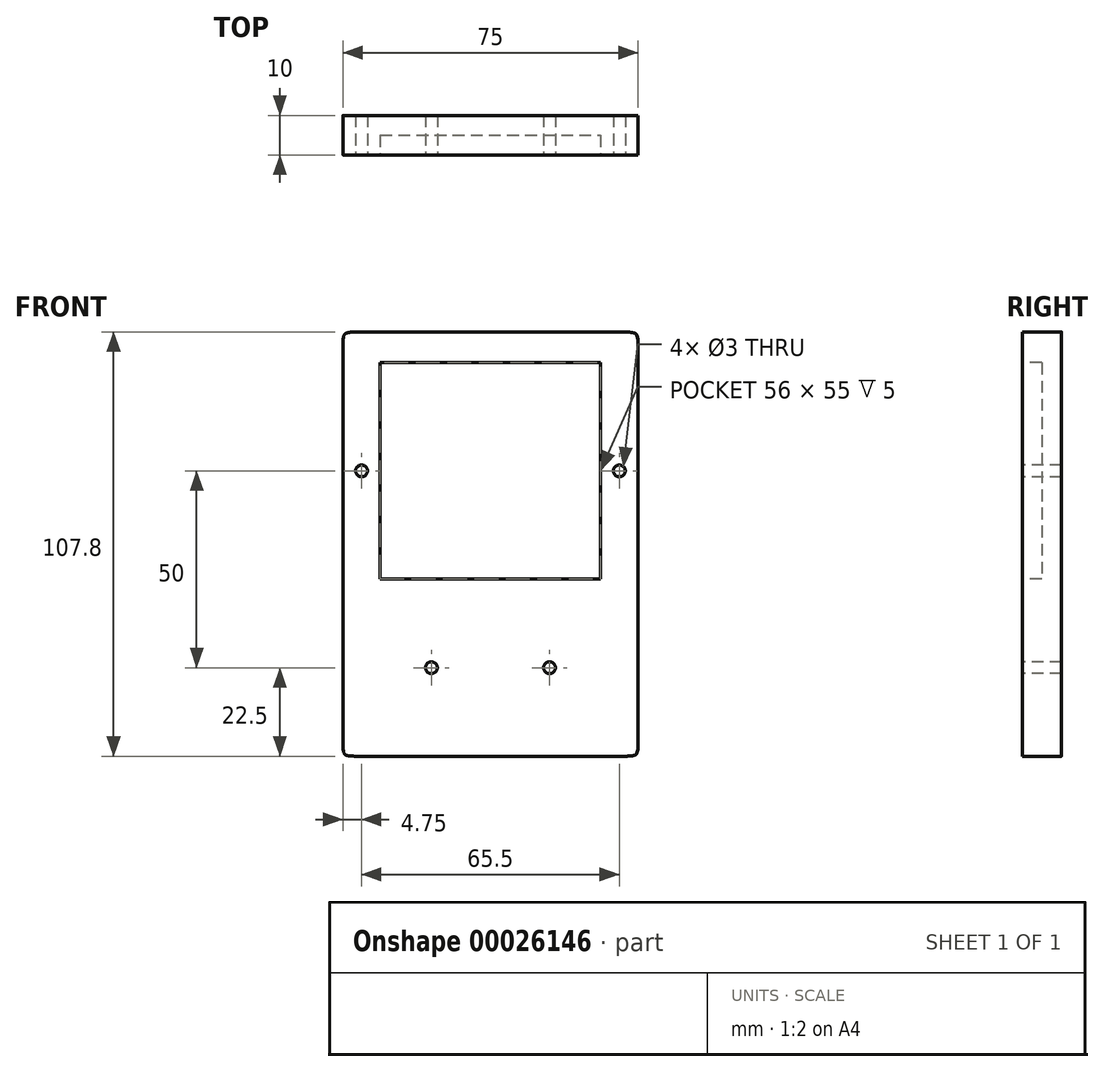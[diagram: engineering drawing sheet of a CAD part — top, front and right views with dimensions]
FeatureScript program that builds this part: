
annotation { "Feature Type Name" : "Feature", "Feature Type Description" : "" }
export const myFeature = defineFeature(function(context is Context, id is Id, definition is map)
    precondition{}
    {
        {
            var Q0;
            Q0=qCreatedBy(makeId("Front.planeOp"),FACE);
            var sketch = newSketch(context, id + "F0", { "sketchPlane" : qUnion([Q0])});
            skLineSegment(sketch, "E0.rect.top", {"start": v(37.5, 53.9) * mm, "end": v(-37.5, 53.9) * mm});
            skLineSegment(sketch, "E0.rect.left", {"start": v(37.5, -53.9) * mm, "end": v(37.5, 53.9) * mm});
            skLineSegment(sketch, "E0.rect.right", {"start": v(-37.5, -53.9) * mm, "end": v(-37.5, 53.9) * mm});
            skPoint(sketch, "E0.rect.middle", {"position": v(0, 0) * mm});
            skLineSegment(sketch, "E1", {"start": v(-37.5, 44.37) * mm, "end": v(37.5, 44.37) * mm, "construction": true});
            skLineSegment(sketch, "E2", {"start": v(37.5, 44.37) * mm, "end": v(-37.5, -44.37) * mm, "construction": true});
            skLineSegment(sketch, "E3", {"start": v(-37.5, -44.37) * mm, "end": v(37.5, -44.37) * mm, "construction": true});
            skPoint(sketch, "E4.rect.middle", {"position": v(-19.5, 44.37) * mm});
            skPoint(sketch, "E5.rect.middle", {"position": v(19.5, 44.37) * mm});
            skPoint(sketch, "E6.rect.middle", {"position": v(-19.5, -44.37) * mm});
            skPoint(sketch, "E7.rect.middle", {"position": v(19.5, -44.37) * mm});
            skLineSegment(sketch, "E8", {"start": v(0, -25) * mm, "end": v(0, 25) * mm, "construction": true});
            skLineSegment(sketch, "E9", {"start": v(-15, 0) * mm, "end": v(15, 0) * mm, "construction": true});
            skPoint(sketch, "E10.rect.middle", {"position": v(25.15, 0) * mm});
            skPoint(sketch, "E11.orphan", {"position": v(20.1, 30.91) * mm});
            skPoint(sketch, "E10.rect.right.end.orphan", {"position": v(30.2, 30.91) * mm});
            skPoint(sketch, "E10.rect.bottom.end.orphan", {"position": v(30.2, -30.91) * mm});
            skPoint(sketch, "E10.rect.bottom.start.orphan", {"position": v(20.1, -30.91) * mm});
            skPoint(sketch, "E12.rect.middle", {"position": v(25.15, -0.46) * mm});
            skPoint(sketch, "E13.center.orphan", {"position": v(20.1, -31.37) * mm});
            skPoint(sketch, "E14.center.orphan", {"position": v(30.2, -31.37) * mm});
            skPoint(sketch, "E15.orphan", {"position": v(-4.5, 40.24) * mm});
            skPoint(sketch, "E4.rect.top.start.orphan", {"position": v(-4.5, 48.5) * mm});
            skPoint(sketch, "E16.orphan", {"position": v(-34.5, 48.5) * mm});
            skPoint(sketch, "E4.rect.right.start.orphan", {"position": v(-34.5, 40.25) * mm});
            skPoint(sketch, "E5.rect.top.start.orphan", {"position": v(4.5, 48.5) * mm});
            skPoint(sketch, "E17.orphan", {"position": v(4.5, 40.24) * mm});
            skPoint(sketch, "E18.orphan", {"position": v(34.5, 48.5) * mm});
            skPoint(sketch, "E5.rect.bottom.end.orphan", {"position": v(34.5, 40.24) * mm});
            skPoint(sketch, "E19.orphan", {"position": v(-4.5, -48.5) * mm});
            skPoint(sketch, "E6.rect.left.end.orphan", {"position": v(-4.5, -40.25) * mm});
            skPoint(sketch, "E20.orphan", {"position": v(-34.5, -40.25) * mm});
            skPoint(sketch, "E6.rect.right.start.orphan", {"position": v(-34.5, -48.5) * mm});
            skPoint(sketch, "E7.rect.right.end.orphan", {"position": v(4.5, -40.24) * mm});
            skPoint(sketch, "E21.trimOffspring.end.orphan", {"position": v(4.5, -48.5) * mm});
            skPoint(sketch, "E22.orphan", {"position": v(34.5, -48.5) * mm});
            skPoint(sketch, "E7.rect.top.start.orphan", {"position": v(34.5, -40.24) * mm});
            skLineSegment(sketch, "E23.rect.bottom", {"start": v(-28, 46.1) * mm, "end": v(28, 46.1) * mm});
            skLineSegment(sketch, "E23.rect.left", {"start": v(-28, 46.1) * mm, "end": v(-28, -8.9) * mm});
            skPoint(sketch, "E23.rect.middle", {"position": v(0, 18.6) * mm});
            skPoint(sketch, "E24.center.orphan", {"position": v(20.1, 30.45) * mm});
            skPoint(sketch, "E25.center.orphan", {"position": v(30.2, 30.45) * mm});
            skLineSegment(sketch, "E26", {"start": v(37.5, 18.6) * mm, "end": v(-37.5, 18.6) * mm, "construction": true});
            skLineSegment(sketch, "E27", {"start": v(-37.5, 18.6) * mm, "end": v(-28, 18.6) * mm, "construction": true});
            skCircle(sketch, "E28", {"center": v(-32.75, 18.6) * mm, "radius": 1.5 * mm});
            skCircle(sketch, "E29.MirrorC", {"center": v(32.75, 18.6) * mm, "radius": 1.5 * mm});
            skLineSegment(sketch, "E30", {"start": v(-28, -8.9) * mm, "end": v(28, -53.9) * mm, "construction": true});
            skPoint(sketch, "E31.start.orphan", {"position": v(28, -8.9) * mm});
            skPoint(sketch, "E0.rect.bottom.end.orphan", {"position": v(30.2, -53.9) * mm});
            skLineSegment(sketch, "E32", {"start": v(28, 46.1) * mm, "end": v(28, -8.9) * mm});
            skLineSegment(sketch, "E33", {"start": v(28, -8.9) * mm, "end": v(-28, -8.9) * mm});
            skLineSegment(sketch, "E34", {"start": v(-37.5, -53.9) * mm, "end": v(37.5, -53.9) * mm});
            skLineSegment(sketch, "E35", {"start": v(-28, 46.1) * mm, "end": v(-37.5, 53.9) * mm, "construction": true});
            skLineSegment(sketch, "E36", {"start": v(28, 46.1) * mm, "end": v(37.5, 53.9) * mm, "construction": true});
            skLineSegment(sketch, "E37", {"start": v(0, -8.9) * mm, "end": v(0, -53.9) * mm, "construction": true});
            skLineSegment(sketch, "E38", {"start": v(0, -31.4) * mm, "end": v(-37.5, -31.4) * mm, "construction": true});
            skCircle(sketch, "E39", {"center": v(-15, -31.4) * mm, "radius": 1.5 * mm});
            skPoint(sketch, "E40.center.orphan", {"position": v(-18.75, -31.4) * mm});
            skCircle(sketch, "E41.MirrorC", {"center": v(15, -31.4) * mm, "radius": 1.5 * mm});
            skSolve(sketch);
        }
        {
            var Q0;
            Q0=makeQuery(id+"F0.imprint","IMPRINT",FACE,{"disambiguationData":[TD([[makeQuery(id+"F0.imprint","IMPRINT",EDGE,{"derivedFrom":sQuery(id+"F0.wireOp",EDGE,"E23.rect.bottom")}),-1.0]])]});
            var Q1;
            {var subQ7=sQuery(id+"F0.wireOp",EDGE,"E0.rect.top");Q1=makeQuery(id+"F0.imprint","IMPRINT",FACE,{"disambiguationData":[TD([[makeQuery(id+"F0.imprint","IMPRINT",EDGE,{"derivedFrom":subQ7}),1.0]])]});}
            extrude(context, id + "F1", {"entities" : qUnion([Q0, Q1]), "oppositeDirection" : true, "depth" : 10 * mm});
        }
        {
            var Q0;
            Q0=makeQuery(id+"F1.opExtrude","SWEPT_EDGE",EDGE,{"disambiguationData":[OSD([sQuery(id+"F0.wireOp",EDGE,"E0.rect.top"),sQuery(id+"F0.wireOp",EDGE,"E0.rect.right")])]});
            var Q1;
            Q1=makeQuery(id+"F1.opExtrude","SWEPT_EDGE",EDGE,{"disambiguationData":[OSD([sQuery(id+"F0.wireOp",EDGE,"E0.rect.bottom"),sQuery(id+"F0.wireOp",EDGE,"E0.rect.right")])]});
            var Q2;
            Q2=makeQuery(id+"F1.opExtrude","SWEPT_EDGE",EDGE,{"disambiguationData":[OSD([sQuery(id+"F0.wireOp",EDGE,"E0.rect.bottom"),sQuery(id+"F0.wireOp",EDGE,"E0.rect.left")])]});
            var Q3;
            Q3=makeQuery(id+"F1.opExtrude","SWEPT_EDGE",EDGE,{"disambiguationData":[OSD([sQuery(id+"F0.wireOp",EDGE,"E0.rect.top"),sQuery(id+"F0.wireOp",EDGE,"E0.rect.left")])]});
            var Q4;
            Q4=makeQuery(id+"F1.opExtrude","SWEPT_EDGE",EDGE,{"disambiguationData":[OSD([sQuery(id+"F0.wireOp",EDGE,"427d9130-ed9a-4b5e-adfc-3cf5be296974.trimOffspring"),sQuery(id+"F0.wireOp",EDGE,"dc01f706-e9b0-4246-b6ca-897daf157666.trimOffspring")])]});
            var Q5;
            Q5=makeQuery(id+"F1.opExtrude","SWEPT_EDGE",EDGE,{"disambiguationData":[OSD([sQuery(id+"F0.wireOp",EDGE,"E12.rect.left"),sQuery(id+"F0.wireOp",EDGE,"ba55f82d-07fc-40dc-a4a4-203b08bc8e9c")])]});
            fillet(context, id + "F2", {"entities" : qUnion([Q0, Q1, Q2, Q3, Q4, Q5]), "radius" : 5 * mm, "tangentPropagation" : true, "rho" : 0.8, "crossSection" : FilletCrossSection.CONIC, "allowEdgeOverflow" : false});
        }
        {
            var Q0;
            Q0=makeQuery(id+"F0.imprint","IMPRINT",FACE,{"disambiguationData":[TD([[makeQuery(id+"F0.imprint","IMPRINT",EDGE,{"derivedFrom":sQuery(id+"F0.wireOp",EDGE,"E23.rect.bottom")}),-1.0]])]});
            extrude(context, id + "F3", {"entities" : qUnion([Q0]), "operationType" : NewBodyOperationType.REMOVE, "oppositeDirection" : true, "depth" : 5 * mm});
        }
    });
